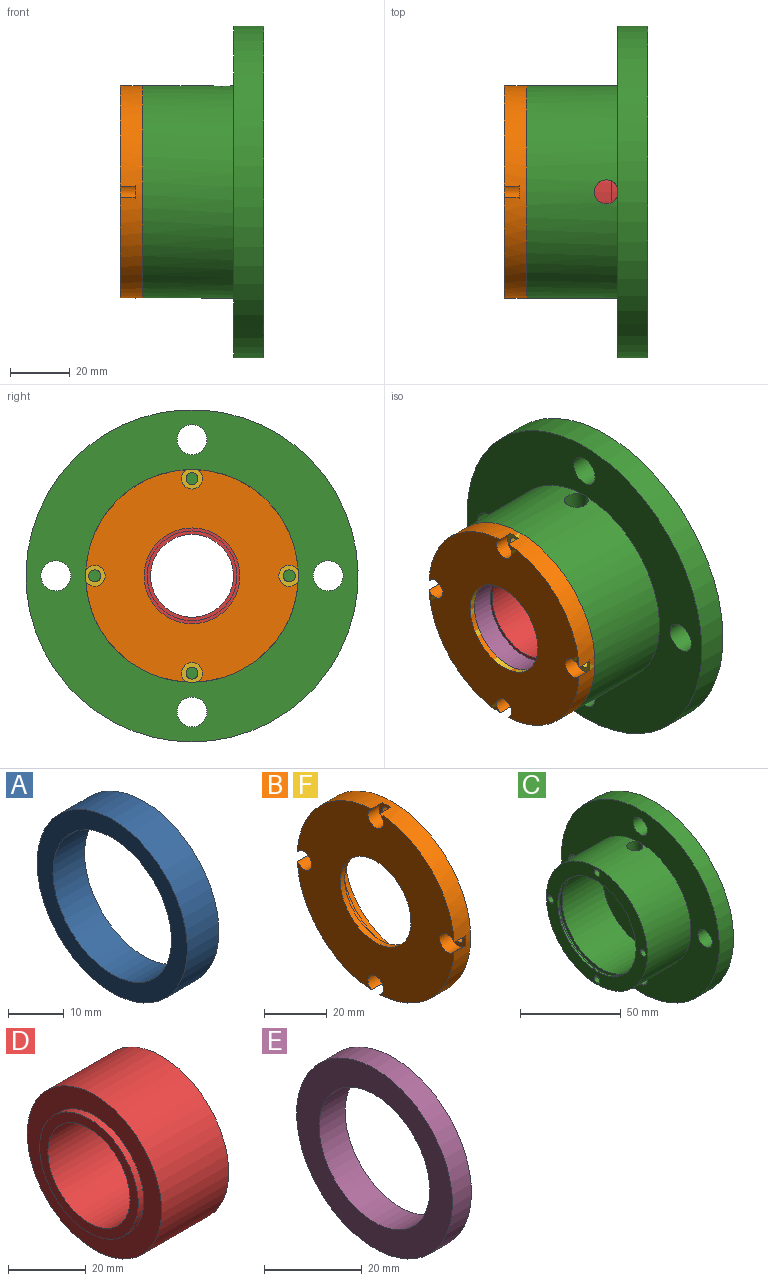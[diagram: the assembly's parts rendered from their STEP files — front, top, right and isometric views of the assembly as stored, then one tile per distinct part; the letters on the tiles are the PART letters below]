
ASSEMBLY  parts=6 mates=3
PART A: 4 faces, bbox 8x38x38 mm
  f0: plane 38x38mm, normal (-1,0,0), area 427.3mm2, adj f1,f3
  f1: cylinder r=15mm len=30mm, axis (-1,0,0), area 754mm2, adj f0,f2
  f2: plane 38x38mm, normal (1,0,0), area 427.3mm2, adj f1,f3
  f3: cylinder r=19mm len=38mm, axis (-1,0,0), area 955mm2, adj f0,f2
PART B: 22 faces, bbox 11.5x71x71 mm
  f0: plane 70.9x70.9mm, normal (-1,0,0), area 3006.1mm2, adj f8,f9,f11,f13,f15,f17
  f1: plane 45x45mm, normal (1,0,0), area 786.2mm2, adj f2,f9
  f2: cylinder r=22.5mm len=45mm, axis (-1,0,0), area 777.5mm2, adj f1,f3
  f3: plane 51x51mm, normal (1,0,0), area 452.4mm2, adj f2,f4
  f4: cylinder r=25.5mm len=51mm, axis (-1,0,0), area 640.9mm2, adj f3,f5
  f5: plane 55x55mm, normal (1,0,0), area 333mm2, adj f4,f6
  f6: cylinder r=27.5mm len=55mm, axis (-1,0,0), area 691.2mm2, adj f5,f7
  f7: plane 71x71mm, normal (1,0,0), area 1533.1mm2, adj f6,f8,f18,f19,f20,f21
  f8: cylinder r=35.5mm len=71mm, axis (-1,0,0), area 1597.5mm2, adj f0,f7,f10,f11,f12,f13,f14,f15
  f9: cylinder r=16mm len=32mm, axis (-1,0,0), area 201.1mm2, adj f0,f1
  f10: plane 7x6.5mm, normal (-1,0,0), area 24.6mm2, adj f8,f11,f21
  f11: cylinder r=3.5mm len=7mm, axis (-1,0,0), area 90.1mm2, adj f0,f8,f10
  f12: plane 7x6.5mm, normal (-1,0,0), area 24.6mm2, adj f8,f13,f20
  f13: cylinder r=3.5mm len=7mm, axis (-1,0,0), area 90.1mm2, adj f0,f8,f12
  f14: plane 7x6.5mm, normal (-1,0,0), area 24.6mm2, adj f8,f15,f19
  f15: cylinder r=3.5mm len=7mm, axis (-1,0,0), area 90.1mm2, adj f0,f8,f14
  f16: plane 7x6.5mm, normal (-1,0,0), area 24.6mm2, adj f8,f17,f18
  f17: cylinder r=3.5mm len=7mm, axis (-1,0,0), area 90.1mm2, adj f0,f8,f16
  f18: cylinder r=2mm len=4mm, axis (-1,0,0), area 31.4mm2, adj f7,f16
  f19: cylinder r=2mm len=4mm, axis (-1,0,0), area 31.4mm2, adj f7,f14
  f20: cylinder r=2mm len=4mm, axis (-1,0,0), area 31.4mm2, adj f7,f12
  f21: cylinder r=2mm len=4mm, axis (-1,0,0), area 31.4mm2, adj f7,f10
PART C: 32 faces, bbox 40.5x111x111 mm
  f0: cylinder r=35.5mm len=71mm, axis (-1,0,0), area 6752.9mm2, adj f11,f24,f27
  f1: cylinder r=27.5mm len=55mm, axis (-1,0,0), area 4874mm2, adj f2,f15,f24
  f2: plane 55x55mm, normal (-1,0,0), area 1571.6mm2, adj f1,f3
  f3: cylinder r=16mm len=32mm, axis (-1,0,0), area 100.5mm2, adj f2,f4
  f4: plane 38x38mm, normal (1,0,0), area 329.9mm2, adj f3,f5
  f5: cylinder r=19mm len=38mm, axis (-1,0,0), area 955mm2, adj f4,f6
  f6: plane 63x63mm, normal (1,0,0), area 1983.1mm2, adj f5,f7
  f7: cylinder r=31.5mm len=63mm, axis (-1,0,0), area 336.5mm2, adj f6,f8
  f8: plane 67x67mm, normal (1,0,0), area 408.4mm2, adj f7,f9
  f9: cylinder r=33.5mm len=67mm, axis (-1,0,0), area 357.8mm2, adj f8,f10
  f10: plane 111x111mm, normal (1,0,0), area 5837.1mm2, adj f9,f26,f28,f29,f30,f31
  f11: plane 71x71mm, normal (-1,0,0), area 1533.1mm2, adj f0,f12,f16,f18,f20,f22
  f12: cylinder r=27.5mm len=55mm, axis (-1,0,0), area 172.8mm2, adj f11,f13
  f13: plane 58.4x58.4mm, normal (1,0,0), area 302.8mm2, adj f12,f14
  f14: cylinder r=29.2mm len=58.4mm, axis (-1,0,0), area 366.9mm2, adj f13,f15
  f15: plane 58.4x58.4mm, normal (-1,0,0), area 302.8mm2, adj f1,f14
  f16: cylinder r=2mm len=20mm, axis (-1,0,0), area 251.3mm2, adj f11,f17
  f17: plane 4x4mm, normal (-1,0,0), area 12.6mm2, adj f16
  f18: cylinder r=2mm len=20mm, axis (-1,0,0), area 251.3mm2, adj f11,f19
  f19: plane 4x4mm, normal (-1,0,0), area 12.6mm2, adj f18
  f20: cylinder r=2mm len=20mm, axis (-1,0,0), area 251.3mm2, adj f11,f21
  f21: plane 4x4mm, normal (-1,0,0), area 12.6mm2, adj f20
  f22: cylinder r=2mm len=20mm, axis (-1,0,0), area 251.3mm2, adj f11,f23
  f23: plane 4x4mm, normal (-1,0,0), area 12.6mm2, adj f22
  f24: cylinder r=4mm len=8.29mm, axis (0,0,-1), area 201.9mm2, adj f0,f1,f25
  f25: cylinder r=35.5mm len=1.91mm, axis (1,0,0), area 0.1mm2, adj f24,f27
  f26: cylinder r=55.5mm len=111mm, axis (1,0,0), area 3487.2mm2, adj f10,f27
  f27: plane 111x111mm, normal (-1,0,0), area 5403.5mm2, adj f0,f25,f26,f28,f29,f30,f31
  f28: cylinder r=5mm len=10mm, axis (-1,0,0), area 314.2mm2, adj f10,f27
  f29: cylinder r=5mm len=10mm, axis (-1,0,0), area 314.2mm2, adj f10,f27
  f30: cylinder r=5mm len=10mm, axis (-1,0,0), area 314.2mm2, adj f10,f27
  f31: cylinder r=5mm len=10mm, axis (-1,0,0), area 314.2mm2, adj f10,f27
PART D: 10 faces, bbox 28.5x49x49 mm
  f0: plane 36x36mm, normal (-1,0,0), area 311mm2, adj f1,f9
  f1: cylinder r=15mm len=30mm, axis (-1,0,0), area 2497.6mm2, adj f0,f2
  f2: plane 30x30mm, normal (-1,0,0), area 104.8mm2, adj f1,f3
  f3: cylinder r=13.84mm len=27.69mm, axis (-1,0,0), area 174mm2, adj f2,f4
  f4: plane 36.68x36.68mm, normal (1,0,0), area 454.8mm2, adj f3,f5
  f5: cylinder r=18.34mm len=36.68mm, axis (-1,0,0), area 230.5mm2, adj f4,f6
  f6: plane 49x49mm, normal (1,0,0), area 828.8mm2, adj f5,f7
  f7: cylinder r=24.5mm len=49mm, axis (-1,0,0), area 3771.5mm2, adj f6,f8
  f8: plane 49x49mm, normal (-1,0,0), area 867.9mm2, adj f7,f9
  f9: cylinder r=18mm len=36mm, axis (-1,0,0), area 226.2mm2, adj f0,f8
PART E: 6 faces, bbox 7.5x45x45 mm
  f0: plane 39x39mm, normal (1,0,0), area 390.3mm2, adj f1,f5
  f1: cylinder r=19.5mm len=39mm, axis (-1,0,0), area 245mm2, adj f0,f2
  f2: plane 45x45mm, normal (1,0,0), area 395.8mm2, adj f1,f3
  f3: cylinder r=22.5mm len=45mm, axis (-1,0,0), area 777.5mm2, adj f2,f4
  f4: plane 45x45mm, normal (-1,0,0), area 786.2mm2, adj f3,f5
  f5: cylinder r=16mm len=32mm, axis (-1,0,0), area 754mm2, adj f0,f4
PART F: same geometry as B
PLACE A t=(-71.89,-13.57,-5.4)mm
PLACE B t=(-32.37,-13.57,-5.4)mm
PLACE C t=(-54.6,-13.57,-5.4)mm
PLACE D t=(-54.37,-13.57,-5.4)mm
PLACE E t=(-48.81,-13.57,-5.4)mm
PLACE F t=(-32.37,-13.57,-5.4)mm
MATE fastened A.f1 <-> C.f0  axis (-1,0,0) through (-21.03,-13.57,-5.4)mm
MATE fastened E.f1 <-> F.f2  axis (-1,0,0) through (-56.28,-13.57,-5.4)mm
MATE fastened D.f1 <-> C.f26  axis (1,0,0) through (-25.03,-13.57,-5.4)mm
